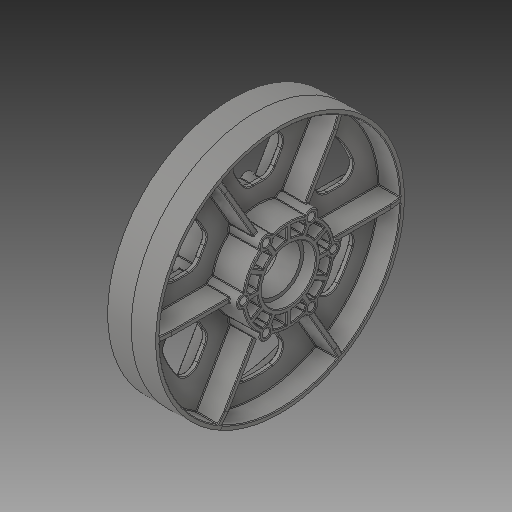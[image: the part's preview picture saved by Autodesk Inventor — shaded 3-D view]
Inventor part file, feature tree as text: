
AUTODESK INVENTOR PART (.ipt)
format: ipt  version: 2018 (Build 220112000, 112)  size: 4,141,568 bytes
history: native  units: in
note: dims shown in document units (in); Inventor stores cm internally (conversion verified against a paired STEP export)
features: fillet x1
ambient origin geometry x8: Origin, YZ Plane, XZ Plane, XY Plane, X Axis, Y Axis, Z Axis, Center Point
bodies: Solid1 (feature_tree)
feature tree (1):
  fillet  "Fillet14"  [1 undecoded]
note: 1 required parameter value undecoded (feature->parameter linkage not recoverable at this tier; creation-order binding heuristic only, values carry confidence <= 0.55)
